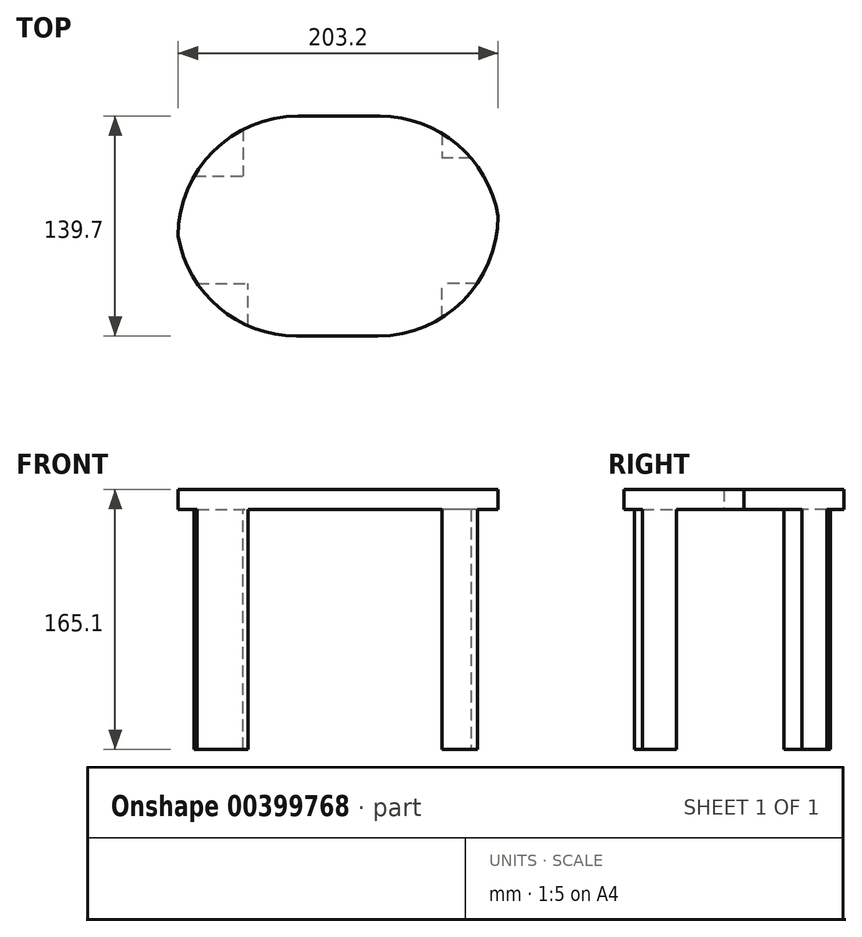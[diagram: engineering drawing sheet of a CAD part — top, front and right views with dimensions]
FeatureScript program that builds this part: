
annotation { "Feature Type Name" : "Feature", "Feature Type Description" : "" }
export const myFeature = defineFeature(function(context is Context, id is Id, definition is map)
    precondition{}
    {
        {
            var Q0;
            Q0=qCreatedBy(makeId("Top.planeOp"),FACE);
            var sketch = newSketch(context, id + "F0", { "sketchPlane" : qUnion([Q0])});
            skLineSegment(sketch, "E0.bottom", {"start": v(-112.77, 74.23) * mm, "end": v(90.43, 74.23) * mm});
            skLineSegment(sketch, "E0.top", {"start": v(-112.77, -65.47) * mm, "end": v(90.43, -65.47) * mm});
            skLineSegment(sketch, "E0.left", {"start": v(-112.77, 74.23) * mm, "end": v(-112.77, -65.47) * mm});
            skLineSegment(sketch, "E0.right", {"start": v(90.43, 74.23) * mm, "end": v(90.43, -65.47) * mm});
            skSolve(sketch);
        }
        {
            var Q0;
            Q0 = qSketchRegion(id + "F0", true);
            extrude(context, id + "F1", {"entities" : qUnion([Q0]), "depth" : 12.7 * mm});
        }
        {
            var Q0;
            Q0=makeQuery(id+"F1.opExtrude","CAP_FACE",FACE,{"disambiguationData":[OSD([sQuery(id+"F0.wireOp",EDGE,"E0.bottom"),sQuery(id+"F0.wireOp",EDGE,"E0.top"),sQuery(id+"F0.wireOp",EDGE,"E0.left"),sQuery(id+"F0.wireOp",EDGE,"E0.right")])],"isStart":true});
            var sketch = newSketch(context, id + "F2", { "sketchPlane" : qUnion([Q0])});
            skLineSegment(sketch, "E1.bottom", {"start": v(90.43, 65.47) * mm, "end": v(54.7, 65.47) * mm});
            skLineSegment(sketch, "E1.top", {"start": v(90.43, 32.06) * mm, "end": v(54.7, 32.06) * mm});
            skLineSegment(sketch, "E1.left", {"start": v(90.43, 65.47) * mm, "end": v(90.43, 32.06) * mm});
            skLineSegment(sketch, "E1.right", {"start": v(54.7, 65.47) * mm, "end": v(54.7, 32.06) * mm});
            skLineSegment(sketch, "E2.bottom", {"start": v(-112.77, 65.47) * mm, "end": v(-68.4, 65.47) * mm});
            skLineSegment(sketch, "E2.top", {"start": v(-112.77, 32.06) * mm, "end": v(-68.4, 32.06) * mm});
            skLineSegment(sketch, "E2.left", {"start": v(-112.77, 65.47) * mm, "end": v(-112.77, 32.06) * mm});
            skLineSegment(sketch, "E2.right", {"start": v(-68.4, 65.47) * mm, "end": v(-68.4, 32.06) * mm});
            skLineSegment(sketch, "E3.bottom", {"start": v(-112.77, -74.23) * mm, "end": v(-71.52, -74.23) * mm});
            skLineSegment(sketch, "E3.top", {"start": v(-112.77, -36.14) * mm, "end": v(-71.52, -36.14) * mm});
            skLineSegment(sketch, "E3.left", {"start": v(-112.77, -74.23) * mm, "end": v(-112.77, -36.14) * mm});
            skLineSegment(sketch, "E3.right", {"start": v(-71.52, -74.23) * mm, "end": v(-71.52, -36.14) * mm});
            skLineSegment(sketch, "E4.bottom", {"start": v(90.43, -74.23) * mm, "end": v(54.7, -74.23) * mm});
            skLineSegment(sketch, "E4.top", {"start": v(90.43, -47.58) * mm, "end": v(54.7, -47.58) * mm});
            skLineSegment(sketch, "E4.left", {"start": v(90.43, -74.23) * mm, "end": v(90.43, -47.58) * mm});
            skLineSegment(sketch, "E4.right", {"start": v(54.7, -74.23) * mm, "end": v(54.7, -47.58) * mm});
            skSolve(sketch);
        }
        {
            var Q0;
            Q0 = qSketchRegion(id + "F2", true);
            extrude(context, id + "F3", {"entities" : qUnion([Q0]), "operationType" : NewBodyOperationType.ADD, "depth" : 152.4 * mm});
        }
        {
            var Q0;
            Q0=makeQuery(id+"F3.boolean.opBoolean","MERGE",EDGE,{"derivedFrom":[makeQuery(id+"F1.opExtrude","SWEPT_EDGE",EDGE,{"disambiguationData":[OSD([sQuery(id+"F0.wireOp",EDGE,"E0.top"),sQuery(id+"F0.wireOp",EDGE,"E0.right")])]}),makeQuery(id+"F3.opExtrude","SWEPT_EDGE",EDGE,{"disambiguationData":[OSD([sQuery(id+"F2.wireOp",EDGE,"E1.bottom"),sQuery(id+"F2.wireOp",EDGE,"E1.left")])]})]});
            fillet(context, id + "F4", {"entities" : qUnion([Q0]), "radius" : 76.2 * mm, "tangentPropagation" : true, "allowEdgeOverflow" : false});
        }
        {
            var Q0;
            Q0=makeQuery(id+"F3.boolean.opBoolean","MERGE",EDGE,{"derivedFrom":[makeQuery(id+"F1.opExtrude","SWEPT_EDGE",EDGE,{"disambiguationData":[OSD([sQuery(id+"F0.wireOp",EDGE,"E0.bottom"),sQuery(id+"F0.wireOp",EDGE,"E0.right")])]}),makeQuery(id+"F3.opExtrude","SWEPT_EDGE",EDGE,{"disambiguationData":[OSD([sQuery(id+"F2.wireOp",EDGE,"E4.bottom"),sQuery(id+"F2.wireOp",EDGE,"E4.left")])]})]});
            fillet(context, id + "F5", {"entities" : qUnion([Q0]), "radius" : 76.2 * mm, "tangentPropagation" : true, "allowEdgeOverflow" : false});
        }
        {
            var Q0;
            Q0=makeQuery(id+"F3.boolean.opBoolean","MERGE",EDGE,{"derivedFrom":[makeQuery(id+"F1.opExtrude","SWEPT_EDGE",EDGE,{"disambiguationData":[OSD([sQuery(id+"F0.wireOp",EDGE,"E0.bottom"),sQuery(id+"F0.wireOp",EDGE,"E0.left")])]}),makeQuery(id+"F3.opExtrude","SWEPT_EDGE",EDGE,{"disambiguationData":[OSD([sQuery(id+"F2.wireOp",EDGE,"E3.bottom"),sQuery(id+"F2.wireOp",EDGE,"E3.left")])]})]});
            fillet(context, id + "F6", {"entities" : qUnion([Q0]), "radius" : 76.2 * mm, "tangentPropagation" : true, "allowEdgeOverflow" : false});
        }
        {
            var Q0;
            Q0=makeQuery(id+"F3.boolean.opBoolean","MERGE",EDGE,{"derivedFrom":[makeQuery(id+"F1.opExtrude","SWEPT_EDGE",EDGE,{"disambiguationData":[OSD([sQuery(id+"F0.wireOp",EDGE,"E0.top"),sQuery(id+"F0.wireOp",EDGE,"E0.left")])]}),makeQuery(id+"F3.opExtrude","SWEPT_EDGE",EDGE,{"disambiguationData":[OSD([sQuery(id+"F2.wireOp",EDGE,"E2.bottom"),sQuery(id+"F2.wireOp",EDGE,"E2.left")])]})]});
            fillet(context, id + "F7", {"entities" : qUnion([Q0]), "radius" : 76.2 * mm, "tangentPropagation" : true, "allowEdgeOverflow" : false});
        }
    });
